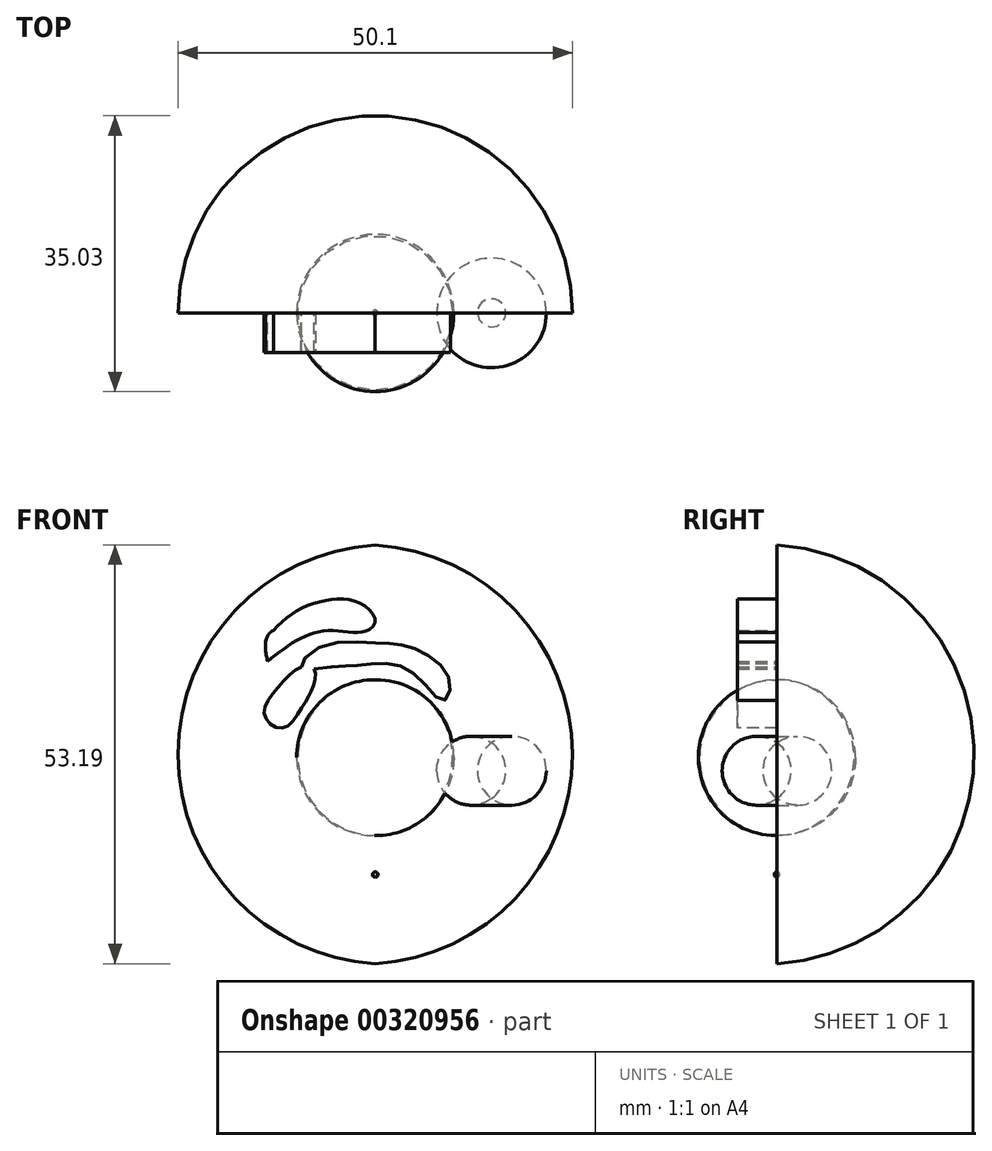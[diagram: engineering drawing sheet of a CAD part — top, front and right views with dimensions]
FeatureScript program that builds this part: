
annotation { "Feature Type Name" : "Feature", "Feature Type Description" : "" }
export const myFeature = defineFeature(function(context is Context, id is Id, definition is map)
    precondition{}
    {
        {
            var Q0;
            Q0=qCreatedBy(makeId("Front.planeOp"),FACE);
            var sketch = newSketch(context, id + "F0", { "sketchPlane" : qUnion([Q0])});
            skLineSegment(sketch, "E0", {"start": v(0, 0) * mm, "end": v(0, 53.19) * mm});
            skArc(sketch, "E1", {"start": v(0, 0) * mm, "mid": v(25.05, 26.6) * mm, "end": v(0, 53.19) * mm});
            skSolve(sketch);
        }
        {
            var Q0;
            Q0 = qSketchRegion(id + "F0", true);
            var Q1;
            Q1=sQuery(id+"F0.wireOp",EDGE,"E0");
            revolve(context, id + "F1", {"entities" : qUnion([Q0]), "axis" : qUnion([Q1]), "revolveType" : RevolveType.ONE_DIRECTION, "angle" : 180 * degree});
        }
        {
            var Q0;
            Q0=qCreatedBy(makeId("Front.planeOp"),FACE);
            var sketch = newSketch(context, id + "F2", { "sketchPlane" : qUnion([Q0])});
            skLineSegment(sketch, "E2", {"start": v(0, 16.28) * mm, "end": v(0, 36.08) * mm});
            skArc(sketch, "E3", {"start": v(0, 16.28) * mm, "mid": v(9.82, 26.18) * mm, "end": v(0, 36.08) * mm});
            skSolve(sketch);
        }
        {
            var Q0;
            Q0 = qSketchRegion(id + "F2", true);
            var Q1;
            Q1=sQuery(id+"F2.wireOp",EDGE,"E2");
            revolve(context, id + "F3", {"entities" : qUnion([Q0]), "axis" : qUnion([Q1]), "revolveType" : RevolveType.FULL});
        }
        {
            var Q0;
            Q0=makeQuery(id+"F1.opRevolve","CAP_FACE",FACE,{"disambiguationData":[OSD([sQuery(id+"F0.wireOp",EDGE,"E0"),sQuery(id+"F0.wireOp",EDGE,"E1")])],"isStart":false});
            var sketch = newSketch(context, id + "F4", { "sketchPlane" : qUnion([Q0])});
            skSolve(sketch);
        }
        {
            var Q0;
            {var subQ0=sQuery(id+"F0.wireOp",EDGE,"E1");Q0=makeQuery(id+"F4.imprint","IMPRINT",FACE,{"disambiguationData":[TD([[makeQuery(id+"F4.imprint","IMPRINT",EDGE,{"derivedFrom":makeQuery(id+"F1.opRevolve","CAP_EDGE",EDGE,{"disambiguationData":[OSD([subQ0])],"isStart":true})}),1.0]])]});}
            var sketch = newSketch(context, id + "F5", { "sketchPlane" : qUnion([Q0])});
            skLineSegment(sketch, "E4", {"start": v(0, 11.65) * mm, "end": v(0, 11) * mm});
            skArc(sketch, "E5", {"start": v(0, 11.65) * mm, "mid": v(-0.3, 11.33) * mm, "end": v(0, 11) * mm});
            skSolve(sketch);
        }
        {
            var Q0;
            Q0 = qSketchRegion(id + "F5", true);
            var Q1;
            Q1=sQuery(id+"F5.wireOp",EDGE,"E4");
            revolve(context, id + "F6", {"entities" : qUnion([Q0]), "axis" : qUnion([Q1]), "revolveType" : RevolveType.FULL});
        }
        {
            var Q0;
            {var subQ0=sQuery(id+"F0.wireOp",EDGE,"E1");Q0=makeQuery(id+"F4.imprint","IMPRINT",FACE,{"disambiguationData":[TD([[makeQuery(id+"F4.imprint","IMPRINT",EDGE,{"derivedFrom":makeQuery(id+"F1.opRevolve","CAP_EDGE",EDGE,{"disambiguationData":[OSD([subQ0])],"isStart":true})}),1.0]])]});}
            var sketch = newSketch(context, id + "F7", { "sketchPlane" : qUnion([Q0])});
            skLineSegment(sketch, "E6", {"start": v(14.77, 28.06) * mm, "end": v(14.77, 20.98) * mm});
            skArc(sketch, "E7", {"start": v(14.77, 20.98) * mm, "mid": v(16.57, 24.52) * mm, "end": v(14.77, 28.06) * mm});
            skSolve(sketch);
        }
        {
            var Q0;
            Q0 = qSketchRegion(id + "F7", true);
            var Q1;
            Q1=sQuery(id+"F7.wireOp",EDGE,"E6");
            revolve(context, id + "F8", {"entities" : qUnion([Q0]), "axis" : qUnion([Q1]), "revolveType" : RevolveType.FULL});
        }
        {
            var Q0;
            {var subQ0=sQuery(id+"F0.wireOp",EDGE,"E1");Q0=makeQuery(id+"F4.imprint","IMPRINT",FACE,{"disambiguationData":[TD([[makeQuery(id+"F4.imprint","IMPRINT",EDGE,{"derivedFrom":makeQuery(id+"F1.opRevolve","CAP_EDGE",EDGE,{"disambiguationData":[OSD([subQ0])],"isStart":true})}),1.0]])]});}
            var sketch = newSketch(context, id + "F9", { "sketchPlane" : qUnion([Q0])});
            skFitSpline(sketch, "E8", {"points": [v(-9.34, 37.7) * mm, v(-5.26, 37.75) * mm, v(-2.15, 37.9) * mm, v(2.13, 38.1) * mm, v(5.93, 35.9) * mm, v(8.7, 33.43) * mm, v(9.55, 35.64) * mm, v(7.08, 38.94) * mm, v(3.37, 40.5) * mm, v(0, 40.75) * mm, v(-7.1, 40.22) * mm, v(-9.34, 37.7) * mm]});
            skFitSpline(sketch, "E9", {"points": [v(-7.9, 35.15) * mm, v(-9.29, 32.58) * mm, v(-11.82, 29.94) * mm, v(-14.06, 31.52) * mm, v(-12.8, 34.57) * mm, v(-9.34, 37.7) * mm, v(-7.77, 37.45) * mm, v(-7.9, 35.15) * mm]});
            skFitSpline(sketch, "E10", {"points": [v(-13.69, 38.43) * mm, v(-9.75, 41.2) * mm, v(-5.68, 42.33) * mm, v(-1.4, 42.2) * mm, v(0, 43.64) * mm, v(-2.2, 45.93) * mm, v(-5.71, 46.24) * mm, v(-9.77, 44.94) * mm, v(-12.94, 42.37) * mm], "startDerivative": vector(27.27, 21.52) * mm, "endDerivative": vector(-22.54, -21.78) * mm});
            skFitSpline(sketch, "E11", {"points": [v(-13.69, 38.43) * mm, v(-12.94, 42.37) * mm, v(2.83, 42.37) * mm, v(5.78, 42.37) * mm, v(9.59, 38.43) * mm, v(11.88, 38.43) * mm, v(12.59, 38.43) * mm, v(10.8, 42.37) * mm, v(6.2, 44.61) * mm, v(1.7, 44.77) * mm], "startDerivative": vector(-8.84, 44.83) * mm, "endDerivative": vector(-39.6, -0.78) * mm});
            skSolve(sketch);
        }
        {
            var Q0;
            Q0 = qSketchRegion(id + "F9", true);
            extrude(context, id + "F10", {"entities" : qUnion([Q0]), "operationType" : NewBodyOperationType.ADD, "depth" : 5 * mm});
        }
    });
